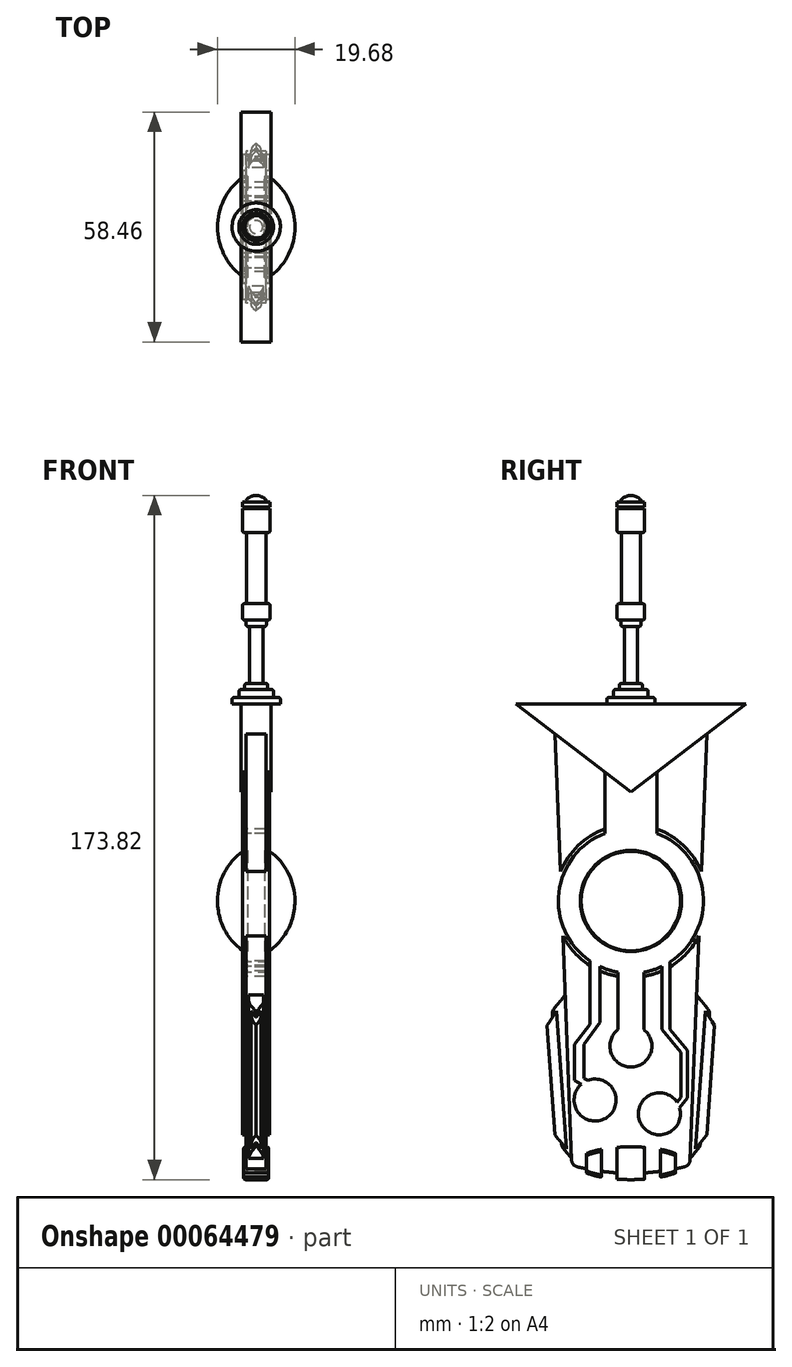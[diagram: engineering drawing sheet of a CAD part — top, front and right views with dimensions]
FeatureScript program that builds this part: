
annotation { "Feature Type Name" : "Feature", "Feature Type Description" : "" }
export const myFeature = defineFeature(function(context is Context, id is Id, definition is map)
    precondition{}
    {
        {
            var Q0;
            Q0=qCreatedBy(makeId("Right.planeOp"),FACE);
            var sketch = newSketch(context, id + "F0", { "sketchPlane" : qUnion([Q0])});
            skLineSegment(sketch, "E0", {"start": v(-29.23, 61.23) * mm, "end": v(0, 61.23) * mm});
            skLineSegment(sketch, "E1", {"start": v(-29.23, 61.23) * mm, "end": v(0, 38.82) * mm});
            skLineSegment(sketch, "E2.MirrorCS", {"start": v(29.23, 61.23) * mm, "end": v(0, 38.82) * mm});
            skLineSegment(sketch, "E3.MirrorCS", {"start": v(29.23, 61.23) * mm, "end": v(0, 61.23) * mm});
            skSolve(sketch);
        }
        {
            var Q0;
            Q0 = qSketchRegion(id + "F0", true);
            var Q1;
            Q1 = qSketchRegion(id + "F13", true);
            extrude(context, id + "F1", {"entities" : qUnion([Q0, Q1]), "endBound" : BoundingType.SYMMETRIC, "depth" : 7.62 * mm});
        }
        {
            var Q0;
            Q0=makeQuery(id+"F1.opExtrude","SWEPT_FACE",FACE,{"disambiguationData":[OSD([sQuery(id+"F0.wireOp",EDGE,"E0"),sQuery(id+"F0.wireOp",EDGE,"E3.MirrorCS")])]});
            var sketch = newSketch(context, id + "F2", { "sketchPlane" : qUnion([Q0])});
            skCircle(sketch, "E4", {"center": v(0, 0) * mm, "radius": 11.71 * mm});
            skSolve(sketch);
        }
        {
            var Q0;
            Q0=qCreatedBy(makeId("Right.planeOp"),FACE);
            var sketch = newSketch(context, id + "F3", { "sketchPlane" : qUnion([Q0])});
            skLineSegment(sketch, "E5", {"start": v(0, -212.2) * mm, "end": v(0, 114.15) * mm});
            skLineSegment(sketch, "E6", {"start": v(-6.14, 61.23) * mm, "end": v(-6.14, 62.83) * mm});
            skLineSegment(sketch, "E7", {"start": v(-6.14, 62.83) * mm, "end": v(-4.4, 62.83) * mm});
            skLineSegment(sketch, "E8", {"start": v(-1.67, 66.45) * mm, "end": v(-1.67, 80.86) * mm});
            skLineSegment(sketch, "E9", {"start": v(-1.67, 80.86) * mm, "end": v(-2.58, 80.86) * mm});
            skLineSegment(sketch, "E10", {"start": v(-2.58, 80.86) * mm, "end": v(-2.58, 82.52) * mm});
            skLineSegment(sketch, "E11", {"start": v(-2.58, 82.52) * mm, "end": v(-3.5, 82.52) * mm});
            skLineSegment(sketch, "E12", {"start": v(-3.5, 82.52) * mm, "end": v(-3.5, 86.7) * mm});
            skLineSegment(sketch, "E13", {"start": v(-3.5, 86.7) * mm, "end": v(-2.45, 86.7) * mm});
            skLineSegment(sketch, "E14", {"start": v(-2.45, 86.7) * mm, "end": v(-2.45, 104.73) * mm});
            skLineSegment(sketch, "E15", {"start": v(-2.45, 104.73) * mm, "end": v(-3.5, 104.73) * mm});
            skLineSegment(sketch, "E16", {"start": v(-3.5, 104.73) * mm, "end": v(-3.5, 110.8) * mm});
            skLineSegment(sketch, "E17", {"start": v(-3.5, 110.8) * mm, "end": v(-2.97, 110.8) * mm});
            skLineSegment(sketch, "E18", {"start": v(-2.97, 110.8) * mm, "end": v(-2.97, 111.21) * mm});
            skLineSegment(sketch, "E19", {"start": v(-2.97, 111.21) * mm, "end": v(-3.5, 111.21) * mm});
            skLineSegment(sketch, "E20", {"start": v(-3.5, 111.21) * mm, "end": v(-3.5, 112.46) * mm});
            skLineSegment(sketch, "E21", {"start": v(-3.5, 112.46) * mm, "end": v(-2.9, 112.46) * mm});
            skArc(sketch, "E22", {"start": v(0, 114.15) * mm, "mid": v(-1.68, 113.7) * mm, "end": v(-2.9, 112.46) * mm});
            skPoint(sketch, "E23.orphan", {"position": v(-3.5, 112.46) * mm});
            skLineSegment(sketch, "E24", {"start": v(-6.14, 61.23) * mm, "end": v(0, 61.23) * mm});
            skLineSegment(sketch, "E25", {"start": v(-2.92, 64.88) * mm, "end": v(-2.92, 66.45) * mm});
            skLineSegment(sketch, "E26", {"start": v(-2.92, 66.45) * mm, "end": v(-1.67, 66.45) * mm});
            skLineSegment(sketch, "E27", {"start": v(-4.4, 62.83) * mm, "end": v(-4.4, 64.88) * mm});
            skLineSegment(sketch, "E28", {"start": v(-4.4, 64.88) * mm, "end": v(-2.92, 64.88) * mm});
            skSolve(sketch);
        }
        {
            var Q0;
            Q0=makeQuery(id+"F3.imprint","IMPRINT",FACE,{"disambiguationData":[TD([[makeQuery(id+"F3.imprint","IMPRINT",EDGE,{"derivedFrom":sQuery(id+"F3.wireOp",EDGE,"E6")}),-1.0]])]});
            var Q1;
            Q1=sQuery(id+"F3.wireOp",EDGE,"E5");
            revolve(context, id + "F4", {"operationType" : NewBodyOperationType.ADD, "entities" : qUnion([Q0]), "axis" : qUnion([Q1]), "revolveType" : RevolveType.FULL});
        }
        {
            var Q0;
            Q0=qCreatedBy(makeId("Right.planeOp"),FACE);
            var sketch = newSketch(context, id + "F5", { "sketchPlane" : qUnion([Q0])});
            skLineSegment(sketch, "E29", {"start": v(-19.3, 53.61) * mm, "end": v(-15, -56.05) * mm});
            skLineSegment(sketch, "E30.MirrorCS", {"start": v(19.3, 53.61) * mm, "end": v(15, -56.05) * mm});
            skLineSegment(sketch, "E31", {"start": v(0, 38.82) * mm, "end": v(-19.3, 53.61) * mm});
            skLineSegment(sketch, "E32", {"start": v(0, 38.82) * mm, "end": v(19.3, 53.61) * mm});
            skArc(sketch, "E33", {"start": v(-15, -56.05) * mm, "mid": v(0, -58.04) * mm, "end": v(15, -56.05) * mm});
            skSolve(sketch);
        }
        {
            var Q0;
            Q0=makeQuery(id+"F5.imprint","IMPRINT",FACE,{"disambiguationData":[TD([[makeQuery(id+"F5.imprint","IMPRINT",EDGE,{"derivedFrom":sQuery(id+"F5.wireOp",EDGE,"E29")}),1.0]])]});
            extrude(context, id + "F6", {"entities" : qUnion([Q0]), "operationType" : NewBodyOperationType.ADD, "endBound" : BoundingType.SYMMETRIC, "depth" : 5.08 * mm});
        }
        {
            var Q0;
            Q0=qCreatedBy(makeId("Right.planeOp"),FACE);
            var sketch = newSketch(context, id + "F7", { "sketchPlane" : qUnion([Q0])});
            skLineSegment(sketch, "E34", {"start": v(-16.7, -12.72) * mm, "end": v(-20.02, -16.87) * mm});
            skLineSegment(sketch, "E35", {"start": v(-20.02, -16.87) * mm, "end": v(-17.57, -51.21) * mm});
            skLineSegment(sketch, "E36", {"start": v(-17.57, -51.21) * mm, "end": v(-15.07, -54.31) * mm});
            skLineSegment(sketch, "E37", {"start": v(-16.7, -12.72) * mm, "end": v(-15.07, -54.31) * mm});
            skLineSegment(sketch, "E38.MirrorCS", {"start": v(16.7, -12.72) * mm, "end": v(20.02, -16.87) * mm});
            skLineSegment(sketch, "E39.MirrorCS", {"start": v(16.7, -12.72) * mm, "end": v(15.07, -54.31) * mm});
            skLineSegment(sketch, "E40.MirrorCS", {"start": v(17.57, -51.21) * mm, "end": v(15.07, -54.31) * mm});
            skLineSegment(sketch, "E41.MirrorCS", {"start": v(20.02, -16.87) * mm, "end": v(17.57, -51.21) * mm});
            skSolve(sketch);
        }
        {
            var Q0;
            Q0 = qSketchRegion(id + "F7", true);
            extrude(context, id + "F8", {"entities" : qUnion([Q0]), "operationType" : NewBodyOperationType.ADD, "endBound" : BoundingType.SYMMETRIC, "depth" : 3.8 * mm});
        }
        {
            var Q0;
            Q0=qCreatedBy(makeId("Right.planeOp"),FACE);
            var sketch = newSketch(context, id + "F9", { "sketchPlane" : qUnion([Q0])});
            skLineSegment(sketch, "E42", {"start": v(-19.9, -18.36) * mm, "end": v(-21.73, -21.25) * mm});
            skLineSegment(sketch, "E43", {"start": v(-19.86, -47.56) * mm, "end": v(-17.64, -50.3) * mm});
            skLineSegment(sketch, "E44", {"start": v(-17.64, -50.3) * mm, "end": v(-19.9, -18.36) * mm});
            skLineSegment(sketch, "E45", {"start": v(-19.86, -47.56) * mm, "end": v(-21.73, -21.25) * mm});
            skLineSegment(sketch, "E46.MirrorCS", {"start": v(19.9, -18.36) * mm, "end": v(21.73, -21.25) * mm});
            skLineSegment(sketch, "E47.MirrorCS", {"start": v(17.64, -50.3) * mm, "end": v(19.9, -18.36) * mm});
            skLineSegment(sketch, "E48.MirrorCS", {"start": v(19.86, -47.56) * mm, "end": v(17.64, -50.3) * mm});
            skLineSegment(sketch, "E49.MirrorCS", {"start": v(19.86, -47.56) * mm, "end": v(21.73, -21.25) * mm});
            skSolve(sketch);
        }
        {
            var Q0;
            Q0=makeQuery(id+"F9.imprint","IMPRINT",FACE,{"disambiguationData":[TD([[makeQuery(id+"F9.imprint","IMPRINT",EDGE,{"derivedFrom":sQuery(id+"F9.wireOp",EDGE,"E42")}),1.0]])]});
            var Q1;
            Q1=makeQuery(id+"F9.imprint","IMPRINT",FACE,{"disambiguationData":[TD([[makeQuery(id+"F9.imprint","IMPRINT",EDGE,{"derivedFrom":sQuery(id+"F9.wireOp",EDGE,"E46.MirrorCS")}),-1.0]])]});
            extrude(context, id + "F10", {"entities" : qUnion([Q0, Q1]), "operationType" : NewBodyOperationType.ADD, "endBound" : BoundingType.SYMMETRIC, "depth" : 2.54 * mm});
        }
        {
            var Q0;
            Q0=qCreatedBy(makeId("Right.planeOp"),FACE);
            var sketch = newSketch(context, id + "F11", { "sketchPlane" : qUnion([Q0])});
            skEllipticalArc(sketch, "E50", {});
            skLineSegment(sketch, "E51", {"start": v(-3.5, -51.45) * mm, "end": v(-3.5, -59.53) * mm});
            skLineSegment(sketch, "E52", {"start": v(0, -51.32) * mm, "end": v(0, -59.66) * mm});
            skLineSegment(sketch, "E53", {"start": v(-7.51, -51.96) * mm, "end": v(-7.51, -59.02) * mm});
            skLineSegment(sketch, "E54", {"start": v(-11.35, -53.04) * mm, "end": v(-11.35, -57.94) * mm});
            skEllipticalArc(sketch, "E55.trimOffspring", {});
            skEllipticalArc(sketch, "E56.trimOffspring", {});
            skEllipticalArc(sketch, "E57.trimOffspring", {});
            skEllipticalArc(sketch, "E58.MirrorCS", {});
            skLineSegment(sketch, "E59.MirrorCS", {"start": v(3.5, -51.45) * mm, "end": v(3.5, -59.53) * mm});
            skEllipticalArc(sketch, "E60.MirrorCS", {});
            skLineSegment(sketch, "E61.MirrorCS", {"start": v(7.51, -51.96) * mm, "end": v(7.51, -59.02) * mm});
            skEllipticalArc(sketch, "E62.MirrorCS", {});
            skLineSegment(sketch, "E63.MirrorCS", {"start": v(11.35, -53.04) * mm, "end": v(11.35, -57.94) * mm});
            skEllipticalArc(sketch, "E64.MirrorCS", {});
            const initialGuessF11  = {"E50": [0, -0.05549049203767605, 1, 0, 0.01403604404596631, 0.004174193487641827, 3.770109793718818, 4.147705169346049], "E55.trimOffspring": [0, -0.05549049203767605, 1, 0, 0.01403604404596631, 0.004174193487641827, 2.135480137833537, 2.5130755134607714], "E56.trimOffspring": [0, -0.05549049203767605, 1, 0, 0.01403604404596631, 0.004174193487641827, 4.460689068859372, 4.71238898038469], "E57.trimOffspring": [0, -0.05549049203767605, 1, 0, 0.01403604404596631, 0.004174193487641827, 1.5707963267948966, 1.8224962383202148], "E58.MirrorCS": [0, -0.05549049203767605, -1, 0, 0.01403604404596631, 0.004174193487641827, 4.460689068859378, 4.71238898038469], "E60.MirrorCS": [0, -0.05549049203767605, -1, 0, 0.01403604404596631, 0.004174193487641827, 1.5707963267948966, 1.822496238320208], "E62.MirrorCS": [0, -0.05549049203767605, -1, 0, 0.01403604404596631, 0.004174193487641827, 3.770109793718824, 4.147705169346056], "E64.MirrorCS": [0, -0.05549049203767605, -1, 0, 0.01403604404596631, 0.004174193487641827, 2.1354801378335297, 2.513075513460759]};
            skSetInitialGuess(sketch, initialGuessF11);
            skSolve(sketch);
        }
        {
            var Q0;
            Q0 = qSketchRegion(id + "F11", true);
            extrude(context, id + "F12", {"entities" : qUnion([Q0]), "operationType" : NewBodyOperationType.ADD, "endBound" : BoundingType.SYMMETRIC, "depth" : 6.35 * mm});
        }
        {
            var Q0;
            Q0=qCreatedBy(makeId("Right.planeOp"),FACE);
            var sketch = newSketch(context, id + "F13", { "sketchPlane" : qUnion([Q0])});
            skCircle(sketch, "E65", {"center": v(0, 11.14) * mm, "radius": 18.41 * mm});
            skLineSegment(sketch, "E66", {"start": v(-6.6, 43.87) * mm, "end": v(-6.6, 28.33) * mm});
            skLineSegment(sketch, "E67.MirrorCS", {"start": v(6.6, 43.87) * mm, "end": v(6.6, 28.33) * mm});
            skLineSegment(sketch, "E68", {"start": v(6.6, 43.87) * mm, "end": v(0, 38.82) * mm});
            skLineSegment(sketch, "E69", {"start": v(0, 38.82) * mm, "end": v(-6.6, 43.87) * mm});
            skSolve(sketch);
        }
        {
            var Q0;
            {var subQ0=sQuery(id+"F5.wireOp",EDGE,"E29");var subQ1=sQuery(id+"F5.wireOp",EDGE,"E33");var subQ2=sQuery(id+"F5.wireOp",EDGE,"E30.MirrorCS");Q0=makeQuery(id+"F19.boolean.opBoolean","SPLIT",FACE,{"disambiguationData":[TD([makeQuery(id+"F6.opExtrude","SWEPT_FACE",FACE,{"disambiguationData":[OSD([subQ1])]})])],"derivedFrom":makeQuery(id+"F6.opExtrude","CAP_FACE",FACE,{"disambiguationData":[OSD([subQ0,subQ2,sQuery(id+"F5.wireOp",EDGE,"E31"),sQuery(id+"F5.wireOp",EDGE,"E32"),subQ1])],"isStart":true})});}
            var sketch = newSketch(context, id + "F14", { "sketchPlane" : qUnion([Q0])});
            skCircle(sketch, "E70", {"center": v(0, 11.14) * mm, "radius": 19.43 * mm});
            skCircle(sketch, "E71", {"center": v(0, 11.14) * mm, "radius": 18.41 * mm});
            skSolve(sketch);
        }
        {
            var Q0;
            Q0 = qSketchRegion(id + "F14", true);
            var Q1;
            {var subQ0=sQuery(id+"F5.wireOp",EDGE,"E29");var subQ1=sQuery(id+"F5.wireOp",EDGE,"E33");var subQ2=sQuery(id+"F5.wireOp",EDGE,"E30.MirrorCS");Q1=makeQuery(id+"F19.boolean.opBoolean","SPLIT",FACE,{"disambiguationData":[TD([makeQuery(id+"F6.opExtrude","SWEPT_FACE",FACE,{"disambiguationData":[OSD([subQ1])]})])],"derivedFrom":makeQuery(id+"F6.opExtrude","CAP_FACE",FACE,{"disambiguationData":[OSD([subQ0,subQ2,sQuery(id+"F5.wireOp",EDGE,"E31"),sQuery(id+"F5.wireOp",EDGE,"E32"),subQ1])],"isStart":false})});}
            extrude(context, id + "F15", {"entities" : qUnion([Q0]), "operationType" : NewBodyOperationType.REMOVE, "endBound" : BoundingType.UP_TO_SURFACE, "oppositeDirection" : true, "endBoundEntityFace" : qUnion([Q1]), "depth" : 25.4 * mm});
        }
        {
            var Q0;
            Q0=qCreatedBy(makeId("Right.planeOp"),FACE);
            var sketch = newSketch(context, id + "F16", { "sketchPlane" : qUnion([Q0])});
            skLineSegment(sketch, "E72", {"start": v(3.3, -6.98) * mm, "end": v(3.3, -21.55) * mm});
            skLineSegment(sketch, "E73.MirrorCS", {"start": v(-3.3, -6.98) * mm, "end": v(-3.3, -21.55) * mm});
            skCircle(sketch, "E74", {"center": v(0, -25.73) * mm, "radius": 5.33 * mm});
            skArc(sketch, "E75", {"start": v(-3.3, -6.98) * mm, "mid": v(0, -7.28) * mm, "end": v(3.3, -6.98) * mm});
            skSolve(sketch);
        }
        {
            var Q0;
            Q0=qCreatedBy(makeId("Right.planeOp"),FACE);
            var sketch = newSketch(context, id + "F17", { "sketchPlane" : qUnion([Q0])});
            skLineSegment(sketch, "E76", {"start": v(-7.83, -5.53) * mm, "end": v(-7.83, -19.77) * mm});
            skLineSegment(sketch, "E77", {"start": v(-7.83, -19.77) * mm, "end": v(-11.97, -25.25) * mm});
            skLineSegment(sketch, "E78", {"start": v(-11.97, -25.25) * mm, "end": v(-11.97, -33.92) * mm});
            skLineSegment(sketch, "E79", {"start": v(-11.97, -33.92) * mm, "end": v(-10.97, -34.46) * mm});
            skLineSegment(sketch, "E80", {"start": v(-12.57, -35.4) * mm, "end": v(-14.32, -34.46) * mm});
            skLineSegment(sketch, "E81", {"start": v(-14.32, -34.46) * mm, "end": v(-14.32, -25.34) * mm});
            skLineSegment(sketch, "E82", {"start": v(-14.32, -25.34) * mm, "end": v(-10.44, -20.2) * mm});
            skLineSegment(sketch, "E83", {"start": v(-10.44, -20.2) * mm, "end": v(-10.44, -4.03) * mm});
            skCircle(sketch, "E84", {"center": v(-9.1, -39.45) * mm, "radius": 5.33 * mm});
            skArc(sketch, "E85", {"start": v(-10.44, -4.03) * mm, "mid": v(-9.17, -4.83) * mm, "end": v(-7.83, -5.53) * mm});
            skSolve(sketch);
        }
        {
            var Q0;
            Q0=qCreatedBy(makeId("Right.planeOp"),FACE);
            var sketch = newSketch(context, id + "F18", { "sketchPlane" : qUnion([Q0])});
            skLineSegment(sketch, "E86", {"start": v(9.94, -4.37) * mm, "end": v(9.94, -21.48) * mm});
            skLineSegment(sketch, "E87", {"start": v(9.94, -21.48) * mm, "end": v(14.37, -26.82) * mm});
            skLineSegment(sketch, "E88", {"start": v(14.37, -26.82) * mm, "end": v(14.37, -38.92) * mm});
            skLineSegment(sketch, "E89", {"start": v(14.37, -38.92) * mm, "end": v(12.38, -41.43) * mm});
            skLineSegment(sketch, "E90", {"start": v(7.83, -5.53) * mm, "end": v(7.83, -21.48) * mm});
            skLineSegment(sketch, "E91", {"start": v(7.83, -21.48) * mm, "end": v(12.72, -27.37) * mm});
            skLineSegment(sketch, "E92", {"start": v(12.72, -27.37) * mm, "end": v(12.72, -38.73) * mm});
            skLineSegment(sketch, "E93", {"start": v(12.72, -38.73) * mm, "end": v(11.7, -40) * mm});
            skCircle(sketch, "E94", {"center": v(7.26, -42.94) * mm, "radius": 5.33 * mm});
            skLineSegment(sketch, "E95", {"start": v(0, -6.18) * mm, "end": v(0, -27.84) * mm, "construction": true});
            skArc(sketch, "E96", {"start": v(7.83, -5.53) * mm, "mid": v(8.9, -4.98) * mm, "end": v(9.94, -4.37) * mm});
            skSolve(sketch);
        }
        {
            var Q0;
            Q0 = qSketchRegion(id + "F18", true);
            var Q1;
            Q1 = qSketchRegion(id + "F17", true);
            var Q2;
            Q2 = qSketchRegion(id + "F16", true);
            var Q3;
            Q3 = qSketchRegion(id + "F13", true);
            extrude(context, id + "F19", {"entities" : qUnion([Q0, Q1, Q2, Q3]), "operationType" : NewBodyOperationType.ADD, "endBound" : BoundingType.SYMMETRIC, "depth" : 6.86 * mm});
        }
        {
            var Q0;
            Q0=makeQuery(id+"F19.boolean.opBoolean","MERGE",FACE,{"derivedFrom":[makeQuery(id+"F19.opExtrude","CAP_FACE",FACE,{"disambiguationData":[OSD([sQuery(id+"F13.wireOp",EDGE,"E65"),sQuery(id+"F13.wireOp",EDGE,"E66"),sQuery(id+"F13.wireOp",EDGE,"E67.MirrorCS"),sQuery(id+"F13.wireOp",EDGE,"E68"),sQuery(id+"F13.wireOp",EDGE,"E69")])],"isStart":false}),makeQuery(id+"F19.opExtrude","CAP_FACE",FACE,{"disambiguationData":[OSD([sQuery(id+"F16.wireOp",EDGE,"E72"),sQuery(id+"F16.wireOp",EDGE,"E73.MirrorCS"),sQuery(id+"F16.wireOp",EDGE,"E74"),sQuery(id+"F16.wireOp",EDGE,"E75")])],"isStart":false}),makeQuery(id+"F19.opExtrude","CAP_FACE",FACE,{"disambiguationData":[OSD([sQuery(id+"F17.wireOp",EDGE,"E76"),sQuery(id+"F17.wireOp",EDGE,"E77"),sQuery(id+"F17.wireOp",EDGE,"E78"),sQuery(id+"F17.wireOp",EDGE,"E79"),sQuery(id+"F17.wireOp",EDGE,"E80"),sQuery(id+"F17.wireOp",EDGE,"E81"),sQuery(id+"F17.wireOp",EDGE,"E82"),sQuery(id+"F17.wireOp",EDGE,"E83"),sQuery(id+"F17.wireOp",EDGE,"E84"),sQuery(id+"F17.wireOp",EDGE,"E85")])],"isStart":false}),makeQuery(id+"F19.opExtrude","CAP_FACE",FACE,{"disambiguationData":[OSD([sQuery(id+"F18.wireOp",EDGE,"E86"),sQuery(id+"F18.wireOp",EDGE,"E87"),sQuery(id+"F18.wireOp",EDGE,"E88"),sQuery(id+"F18.wireOp",EDGE,"E89"),sQuery(id+"F18.wireOp",EDGE,"E90"),sQuery(id+"F18.wireOp",EDGE,"E91"),sQuery(id+"F18.wireOp",EDGE,"E92"),sQuery(id+"F18.wireOp",EDGE,"E93"),sQuery(id+"F18.wireOp",EDGE,"E94"),sQuery(id+"F18.wireOp",EDGE,"E96")])],"isStart":false})]});
            var sketch = newSketch(context, id + "F20", { "sketchPlane" : qUnion([Q0])});
            skCircle(sketch, "E97", {"center": v(0, 11.14) * mm, "radius": 12.64 * mm});
            skSolve(sketch);
        }
        {
            var Q0;
            Q0=qCreatedBy(makeId("Front.planeOp"),FACE);
            var sketch = newSketch(context, id + "F21", { "sketchPlane" : qUnion([Q0])});
            skLineSegment(sketch, "E98", {"start": v(3.43, -1.5) * mm, "end": v(3.43, 11.14) * mm});
            skLineSegment(sketch, "E99", {"start": v(3.43, 11.14) * mm, "end": v(9.84, 11.14) * mm});
            skArc(sketch, "E100", {"start": v(3.43, -1.5) * mm, "mid": v(8.14, 4.05) * mm, "end": v(9.84, 11.14) * mm});
            skSolve(sketch);
        }
        {
            var Q0;
            Q0=makeQuery(id+"F21.imprint","IMPRINT",FACE,{"disambiguationData":[TD([[makeQuery(id+"F21.imprint","IMPRINT",EDGE,{"derivedFrom":sQuery(id+"F21.wireOp",EDGE,"E98")}),-1.0]])]});
            var Q1;
            Q1=sQuery(id+"F21.wireOp",EDGE,"E99");
            revolve(context, id + "F22", {"entities" : qUnion([Q0]), "axis" : qUnion([Q1]), "revolveType" : RevolveType.FULL});
        }
        {
            var Q0;
            Q0=makeQuery(id+"F22.opRevolve","SWEPT_BODY",BODY,{"disambiguationData":[OSD([sQuery(id+"F21.wireOp",EDGE,"E98"),sQuery(id+"F21.wireOp",EDGE,"E99"),sQuery(id+"F21.wireOp",EDGE,"E100")])]});
            var Q1;
            Q1=qCreatedBy(makeId("Right.planeOp"),FACE);
            mirror(context, id + "F23", {"operationType" : NewBodyOperationType.ADD, "entities" : qUnion([Q0]), "mirrorPlane" : qUnion([Q1])});
        }
        {
            var Q0;
            Q0=makeQuery(id+"F19.boolean.opBoolean","MERGE",FACE,{"derivedFrom":[makeQuery(id+"F19.opExtrude","CAP_FACE",FACE,{"disambiguationData":[OSD([sQuery(id+"F13.wireOp",EDGE,"E65"),sQuery(id+"F13.wireOp",EDGE,"E66"),sQuery(id+"F13.wireOp",EDGE,"E67.MirrorCS"),sQuery(id+"F13.wireOp",EDGE,"E68"),sQuery(id+"F13.wireOp",EDGE,"E69")])],"isStart":true}),makeQuery(id+"F19.opExtrude","CAP_FACE",FACE,{"disambiguationData":[OSD([sQuery(id+"F16.wireOp",EDGE,"E72"),sQuery(id+"F16.wireOp",EDGE,"E73.MirrorCS"),sQuery(id+"F16.wireOp",EDGE,"E74"),sQuery(id+"F16.wireOp",EDGE,"E75")])],"isStart":true}),makeQuery(id+"F19.opExtrude","CAP_FACE",FACE,{"disambiguationData":[OSD([sQuery(id+"F17.wireOp",EDGE,"E76"),sQuery(id+"F17.wireOp",EDGE,"E77"),sQuery(id+"F17.wireOp",EDGE,"E78"),sQuery(id+"F17.wireOp",EDGE,"E79"),sQuery(id+"F17.wireOp",EDGE,"E80"),sQuery(id+"F17.wireOp",EDGE,"E81"),sQuery(id+"F17.wireOp",EDGE,"E82"),sQuery(id+"F17.wireOp",EDGE,"E83"),sQuery(id+"F17.wireOp",EDGE,"E84"),sQuery(id+"F17.wireOp",EDGE,"E85")])],"isStart":true}),makeQuery(id+"F19.opExtrude","CAP_FACE",FACE,{"disambiguationData":[OSD([sQuery(id+"F18.wireOp",EDGE,"E86"),sQuery(id+"F18.wireOp",EDGE,"E87"),sQuery(id+"F18.wireOp",EDGE,"E88"),sQuery(id+"F18.wireOp",EDGE,"E89"),sQuery(id+"F18.wireOp",EDGE,"E90"),sQuery(id+"F18.wireOp",EDGE,"E91"),sQuery(id+"F18.wireOp",EDGE,"E92"),sQuery(id+"F18.wireOp",EDGE,"E93"),sQuery(id+"F18.wireOp",EDGE,"E94"),sQuery(id+"F18.wireOp",EDGE,"E96")])],"isStart":true})]});
            var sketch = newSketch(context, id + "F24", { "sketchPlane" : qUnion([Q0])});
            skCircle(sketch, "E101", {"center": v(0, 11.14) * mm, "radius": 12.87 * mm});
            skCircle(sketch, "E102.0", {"center": v(0, 11.14) * mm, "radius": 12.64 * mm});
            skSolve(sketch);
        }
        {
            var Q0;
            Q0 = qSketchRegion(id + "F24", true);
            extrude(context, id + "F25", {"entities" : qUnion([Q0]), "oppositeDirection" : true, "depth" : 1.27 * mm});
        }
        {
            var Q0;
            Q0=makeQuery(id+"F25.opExtrude","SWEPT_BODY",BODY,{"disambiguationData":[OSD([sQuery(id+"F24.wireOp",EDGE,"E101"),sQuery(id+"F24.wireOp",EDGE,"E102.0")])]});
            var Q1;
            Q1=qCreatedBy(makeId("Right.planeOp"),FACE);
            mirror(context, id + "F26", {"operationType" : NewBodyOperationType.REMOVE, "entities" : qUnion([Q0]), "mirrorPlane" : qUnion([Q1])});
        }
        {
            var Q0;
            Q0=makeQuery(id+"F25.opExtrude","SWEPT_BODY",BODY,{"disambiguationData":[OSD([sQuery(id+"F24.wireOp",EDGE,"E101"),sQuery(id+"F24.wireOp",EDGE,"E102.0")])]});
            var Q1;
            Q1=makeQuery(id+"F1.opExtrude","SWEPT_BODY",BODY,{"disambiguationData":[OSD([sQuery(id+"F0.wireOp",EDGE,"E0"),sQuery(id+"F0.wireOp",EDGE,"E2.MirrorCS"),sQuery(id+"F0.wireOp",EDGE,"E1"),sQuery(id+"F0.wireOp",EDGE,"E3.MirrorCS")])]});
            booleanBodies(context, id + "F27", {"operationType" : BooleanOperationType.SUBTRACTION, "tools" : qUnion([Q0]), "targets" : qUnion([Q1])});
        }
        {
            var Q0;
            Q0=makeQuery(id+"F12.opExtrude","CAP_EDGE",EDGE,{"disambiguationData":[OSD([sQuery(id+"F11.wireOp",EDGE,"E56.trimOffspring"),sQuery(id+"F11.wireOp",EDGE,"E60.MirrorCS")])],"isStart":false});
            var Q1;
            Q1=makeQuery(id+"F12.opExtrude","CAP_EDGE",EDGE,{"disambiguationData":[OSD([sQuery(id+"F11.wireOp",EDGE,"E64.MirrorCS")])],"isStart":false});
            var Q2;
            Q2=makeQuery(id+"F12.opExtrude","CAP_EDGE",EDGE,{"disambiguationData":[OSD([sQuery(id+"F11.wireOp",EDGE,"E50")])],"isStart":false});
            var Q3;
            Q3=makeQuery(id+"F12.opExtrude","CAP_EDGE",EDGE,{"disambiguationData":[OSD([sQuery(id+"F11.wireOp",EDGE,"E64.MirrorCS")])],"isStart":true});
            var Q4;
            Q4=makeQuery(id+"F12.opExtrude","CAP_EDGE",EDGE,{"disambiguationData":[OSD([sQuery(id+"F11.wireOp",EDGE,"E56.trimOffspring"),sQuery(id+"F11.wireOp",EDGE,"E60.MirrorCS")])],"isStart":true});
            var Q5;
            Q5=makeQuery(id+"F12.opExtrude","CAP_EDGE",EDGE,{"disambiguationData":[OSD([sQuery(id+"F11.wireOp",EDGE,"E50")])],"isStart":true});
            var Q6;
            Q6=makeQuery(id+"F12.opExtrude","CAP_EDGE",EDGE,{"disambiguationData":[OSD([sQuery(id+"F11.wireOp",EDGE,"E55.trimOffspring")])],"isStart":false});
            var Q7;
            Q7=makeQuery(id+"F12.opExtrude","CAP_EDGE",EDGE,{"disambiguationData":[OSD([sQuery(id+"F11.wireOp",EDGE,"E57.trimOffspring"),sQuery(id+"F11.wireOp",EDGE,"E58.MirrorCS")])],"isStart":false});
            var Q8;
            Q8=makeQuery(id+"F12.opExtrude","CAP_EDGE",EDGE,{"disambiguationData":[OSD([sQuery(id+"F11.wireOp",EDGE,"E62.MirrorCS")])],"isStart":false});
            var Q9;
            Q9=makeQuery(id+"F12.opExtrude","CAP_EDGE",EDGE,{"disambiguationData":[OSD([sQuery(id+"F11.wireOp",EDGE,"E55.trimOffspring")])],"isStart":true});
            var Q10;
            Q10=makeQuery(id+"F12.opExtrude","CAP_EDGE",EDGE,{"disambiguationData":[OSD([sQuery(id+"F11.wireOp",EDGE,"E57.trimOffspring"),sQuery(id+"F11.wireOp",EDGE,"E58.MirrorCS")])],"isStart":true});
            var Q11;
            Q11=makeQuery(id+"F12.opExtrude","CAP_EDGE",EDGE,{"disambiguationData":[OSD([sQuery(id+"F11.wireOp",EDGE,"E62.MirrorCS")])],"isStart":true});
            fillet(context, id + "F28", {"entities" : qUnion([Q0, Q1, Q2, Q3, Q4, Q5, Q6, Q7, Q8, Q9, Q10, Q11]), "radius" : 0.5 * mm, "tangentPropagation" : true, "allowEdgeOverflow" : false});
        }
        {
            var Q0;
            Q0=makeQuery(id+"F10.opExtrude","CAP_EDGE",EDGE,{"disambiguationData":[OSD([sQuery(id+"F9.wireOp",EDGE,"E45")])],"isStart":true});
            var Q1;
            Q1=makeQuery(id+"F10.opExtrude","CAP_EDGE",EDGE,{"disambiguationData":[OSD([sQuery(id+"F9.wireOp",EDGE,"E45")])],"isStart":false});
            var Q2;
            Q2=makeQuery(id+"F10.opExtrude","CAP_EDGE",EDGE,{"disambiguationData":[OSD([sQuery(id+"F9.wireOp",EDGE,"E49.MirrorCS")])],"isStart":true});
            var Q3;
            Q3=makeQuery(id+"F10.opExtrude","CAP_EDGE",EDGE,{"disambiguationData":[OSD([sQuery(id+"F9.wireOp",EDGE,"E49.MirrorCS")])],"isStart":false});
            var Q4;
            Q4=makeQuery(id+"F8.opExtrude","CAP_EDGE",EDGE,{"disambiguationData":[OSD([sQuery(id+"F7.wireOp",EDGE,"E35")])],"isStart":false});
            var Q5;
            Q5=makeQuery(id+"F8.opExtrude","CAP_EDGE",EDGE,{"disambiguationData":[OSD([sQuery(id+"F7.wireOp",EDGE,"E35")])],"isStart":true});
            var Q6;
            Q6=makeQuery(id+"F8.opExtrude","CAP_EDGE",EDGE,{"disambiguationData":[OSD([sQuery(id+"F7.wireOp",EDGE,"E41.MirrorCS")])],"isStart":true});
            var Q7;
            Q7=makeQuery(id+"F8.opExtrude","CAP_EDGE",EDGE,{"disambiguationData":[OSD([sQuery(id+"F7.wireOp",EDGE,"E41.MirrorCS")])],"isStart":false});
            chamfer(context, id + "F29", {"entities" : qUnion([Q0, Q1, Q2, Q3, Q4, Q5, Q6, Q7]), "chamferType" : ChamferType.OFFSET_ANGLE, "width" : 1.78 * mm, "oppositeDirection" : true, "angle" : 45 * degree, "tangentPropagation" : true});
        }
        {
            var Q0;
            Q0=makeQuery(id+"F4.opRevolve","SWEPT_FACE",FACE,{"disambiguationData":[OSD([sQuery(id+"F3.wireOp",EDGE,"E27")])]});
            var Q1;
            Q1=makeQuery(id+"F4.opRevolve","SWEPT_EDGE",EDGE,{"disambiguationData":[OSD([sQuery(id+"F3.wireOp",EDGE,"E6"),sQuery(id+"F3.wireOp",EDGE,"E7")])]});
            var Q2;
            Q2=makeQuery(id+"F4.opRevolve","SWEPT_EDGE",EDGE,{"disambiguationData":[OSD([sQuery(id+"F3.wireOp",EDGE,"E25"),sQuery(id+"F3.wireOp",EDGE,"E26")])]});
            var Q3;
            Q3=makeQuery(id+"F4.opRevolve","SWEPT_EDGE",EDGE,{"disambiguationData":[OSD([sQuery(id+"F3.wireOp",EDGE,"E12"),sQuery(id+"F3.wireOp",EDGE,"E13")])]});
            var Q4;
            Q4=makeQuery(id+"F4.opRevolve","SWEPT_EDGE",EDGE,{"disambiguationData":[OSD([sQuery(id+"F3.wireOp",EDGE,"E11"),sQuery(id+"F3.wireOp",EDGE,"E12")])]});
            var Q5;
            Q5=makeQuery(id+"F4.opRevolve","SWEPT_EDGE",EDGE,{"disambiguationData":[OSD([sQuery(id+"F3.wireOp",EDGE,"E15"),sQuery(id+"F3.wireOp",EDGE,"E16")])]});
            var Q6;
            Q6=makeQuery(id+"F4.opRevolve","SWEPT_EDGE",EDGE,{"disambiguationData":[OSD([sQuery(id+"F3.wireOp",EDGE,"E9"),sQuery(id+"F3.wireOp",EDGE,"E10")])]});
            fillet(context, id + "F30", {"entities" : qUnion([Q0, Q1, Q2, Q3, Q4, Q5, Q6]), "radius" : 0.5 * mm, "tangentPropagation" : true, "allowEdgeOverflow" : false});
        }
        {
            var Q0;
            Q0=makeQuery(id+"F6.opExtrude","SWEPT_EDGE",EDGE,{"disambiguationData":[OSD([sQuery(id+"F5.wireOp",EDGE,"E29"),sQuery(id+"F5.wireOp",EDGE,"E33")])]});
            var Q1;
            Q1=makeQuery(id+"F6.opExtrude","SWEPT_EDGE",EDGE,{"disambiguationData":[OSD([sQuery(id+"F5.wireOp",EDGE,"E30.MirrorCS"),sQuery(id+"F5.wireOp",EDGE,"E33")])]});
            var Q2;
            Q2=makeQuery(id+"F8.opExtrude","SWEPT_EDGE",EDGE,{"disambiguationData":[OSD([sQuery(id+"F7.wireOp",EDGE,"E40.MirrorCS"),sQuery(id+"F7.wireOp",EDGE,"E41.MirrorCS")])]});
            var Q3;
            Q3=makeQuery(id+"F8.opExtrude","SWEPT_EDGE",EDGE,{"disambiguationData":[OSD([sQuery(id+"F7.wireOp",EDGE,"E34"),sQuery(id+"F7.wireOp",EDGE,"E35")])]});
            var Q4;
            Q4=makeQuery(id+"F8.opExtrude","SWEPT_EDGE",EDGE,{"disambiguationData":[OSD([sQuery(id+"F7.wireOp",EDGE,"E38.MirrorCS"),sQuery(id+"F7.wireOp",EDGE,"E41.MirrorCS")])]});
            var Q5;
            Q5=makeQuery(id+"F8.opExtrude","SWEPT_EDGE",EDGE,{"disambiguationData":[OSD([sQuery(id+"F7.wireOp",EDGE,"E35"),sQuery(id+"F7.wireOp",EDGE,"E36")])]});
            var Q6;
            {var subQ0=sQuery(id+"F7.wireOp",EDGE,"E35");Q6=makeQuery(id+"F29.opChamfer","BLEND_EDGE",EDGE,{"blendedFrom":[makeQuery(id+"F8.opExtrude","CAP_EDGE",EDGE,{"disambiguationData":[OSD([subQ0])],"isStart":true}),makeQuery(id+"F8.opExtrude","CAP_FACE",FACE,{"disambiguationData":[OSD([sQuery(id+"F7.wireOp",EDGE,"E34"),subQ0,sQuery(id+"F7.wireOp",EDGE,"E36"),sQuery(id+"F7.wireOp",EDGE,"E37")])],"isStart":true})],"blendedInto":[makeQuery(id+"F8.opExtrude","CAP_FACE",FACE,{"disambiguationData":[OSD([sQuery(id+"F7.wireOp",EDGE,"E34"),subQ0,sQuery(id+"F7.wireOp",EDGE,"E36"),sQuery(id+"F7.wireOp",EDGE,"E37")])],"isStart":true})]});}
            var Q7;
            {var subQ0=sQuery(id+"F9.wireOp",EDGE,"E45");Q7=makeQuery(id+"F29.opChamfer","BLEND_EDGE",EDGE,{"blendedFrom":[makeQuery(id+"F10.opExtrude","CAP_EDGE",EDGE,{"disambiguationData":[OSD([subQ0])],"isStart":true}),makeQuery(id+"F10.opExtrude","CAP_FACE",FACE,{"disambiguationData":[OSD([sQuery(id+"F9.wireOp",EDGE,"E42"),sQuery(id+"F9.wireOp",EDGE,"E43"),sQuery(id+"F9.wireOp",EDGE,"E44"),subQ0])],"isStart":true})],"blendedInto":[makeQuery(id+"F10.opExtrude","CAP_FACE",FACE,{"disambiguationData":[OSD([sQuery(id+"F9.wireOp",EDGE,"E42"),sQuery(id+"F9.wireOp",EDGE,"E43"),sQuery(id+"F9.wireOp",EDGE,"E44"),subQ0])],"isStart":true})]});}
            var Q8;
            {var subQ0=sQuery(id+"F9.wireOp",EDGE,"E45");Q8=makeQuery(id+"F29.opChamfer","BLEND_EDGE",EDGE,{"blendedFrom":[makeQuery(id+"F10.opExtrude","CAP_EDGE",EDGE,{"disambiguationData":[OSD([subQ0])],"isStart":false}),makeQuery(id+"F10.opExtrude","CAP_FACE",FACE,{"disambiguationData":[OSD([sQuery(id+"F9.wireOp",EDGE,"E42"),sQuery(id+"F9.wireOp",EDGE,"E43"),sQuery(id+"F9.wireOp",EDGE,"E44"),subQ0])],"isStart":false})],"blendedInto":[makeQuery(id+"F10.opExtrude","CAP_FACE",FACE,{"disambiguationData":[OSD([sQuery(id+"F9.wireOp",EDGE,"E42"),sQuery(id+"F9.wireOp",EDGE,"E43"),sQuery(id+"F9.wireOp",EDGE,"E44"),subQ0])],"isStart":false})]});}
            var Q9;
            {var subQ0=sQuery(id+"F7.wireOp",EDGE,"E35");Q9=makeQuery(id+"F29.opChamfer","BLEND_EDGE",EDGE,{"blendedFrom":[makeQuery(id+"F8.opExtrude","CAP_EDGE",EDGE,{"disambiguationData":[OSD([subQ0])],"isStart":false}),makeQuery(id+"F8.opExtrude","CAP_FACE",FACE,{"disambiguationData":[OSD([sQuery(id+"F7.wireOp",EDGE,"E34"),subQ0,sQuery(id+"F7.wireOp",EDGE,"E36"),sQuery(id+"F7.wireOp",EDGE,"E37")])],"isStart":false})],"blendedInto":[makeQuery(id+"F8.opExtrude","CAP_FACE",FACE,{"disambiguationData":[OSD([sQuery(id+"F7.wireOp",EDGE,"E34"),subQ0,sQuery(id+"F7.wireOp",EDGE,"E36"),sQuery(id+"F7.wireOp",EDGE,"E37")])],"isStart":false})]});}
            var Q10;
            {var subQ0=sQuery(id+"F7.wireOp",EDGE,"E41.MirrorCS");Q10=makeQuery(id+"F29.opChamfer","BLEND_EDGE",EDGE,{"blendedFrom":[makeQuery(id+"F8.opExtrude","CAP_EDGE",EDGE,{"disambiguationData":[OSD([subQ0])],"isStart":true}),makeQuery(id+"F8.opExtrude","CAP_FACE",FACE,{"disambiguationData":[OSD([sQuery(id+"F7.wireOp",EDGE,"E38.MirrorCS"),sQuery(id+"F7.wireOp",EDGE,"E39.MirrorCS"),sQuery(id+"F7.wireOp",EDGE,"E40.MirrorCS"),subQ0])],"isStart":true})],"blendedInto":[makeQuery(id+"F8.opExtrude","CAP_FACE",FACE,{"disambiguationData":[OSD([sQuery(id+"F7.wireOp",EDGE,"E38.MirrorCS"),sQuery(id+"F7.wireOp",EDGE,"E39.MirrorCS"),sQuery(id+"F7.wireOp",EDGE,"E40.MirrorCS"),subQ0])],"isStart":true})]});}
            var Q11;
            {var subQ0=sQuery(id+"F9.wireOp",EDGE,"E49.MirrorCS");Q11=makeQuery(id+"F29.opChamfer","BLEND_EDGE",EDGE,{"blendedFrom":[makeQuery(id+"F10.opExtrude","CAP_EDGE",EDGE,{"disambiguationData":[OSD([subQ0])],"isStart":true}),makeQuery(id+"F10.opExtrude","CAP_FACE",FACE,{"disambiguationData":[OSD([sQuery(id+"F9.wireOp",EDGE,"E46.MirrorCS"),sQuery(id+"F9.wireOp",EDGE,"E47.MirrorCS"),sQuery(id+"F9.wireOp",EDGE,"E48.MirrorCS"),subQ0])],"isStart":true})],"blendedInto":[makeQuery(id+"F10.opExtrude","CAP_FACE",FACE,{"disambiguationData":[OSD([sQuery(id+"F9.wireOp",EDGE,"E46.MirrorCS"),sQuery(id+"F9.wireOp",EDGE,"E47.MirrorCS"),sQuery(id+"F9.wireOp",EDGE,"E48.MirrorCS"),subQ0])],"isStart":true})]});}
            var Q12;
            {var subQ0=sQuery(id+"F9.wireOp",EDGE,"E49.MirrorCS");Q12=makeQuery(id+"F29.opChamfer","BLEND_EDGE",EDGE,{"blendedFrom":[makeQuery(id+"F10.opExtrude","CAP_EDGE",EDGE,{"disambiguationData":[OSD([subQ0])],"isStart":false}),makeQuery(id+"F10.opExtrude","CAP_FACE",FACE,{"disambiguationData":[OSD([sQuery(id+"F9.wireOp",EDGE,"E46.MirrorCS"),sQuery(id+"F9.wireOp",EDGE,"E47.MirrorCS"),sQuery(id+"F9.wireOp",EDGE,"E48.MirrorCS"),subQ0])],"isStart":false})],"blendedInto":[makeQuery(id+"F10.opExtrude","CAP_FACE",FACE,{"disambiguationData":[OSD([sQuery(id+"F9.wireOp",EDGE,"E46.MirrorCS"),sQuery(id+"F9.wireOp",EDGE,"E47.MirrorCS"),sQuery(id+"F9.wireOp",EDGE,"E48.MirrorCS"),subQ0])],"isStart":false})]});}
            var Q13;
            {var subQ0=sQuery(id+"F7.wireOp",EDGE,"E41.MirrorCS");Q13=makeQuery(id+"F29.opChamfer","BLEND_EDGE",EDGE,{"blendedFrom":[makeQuery(id+"F8.opExtrude","CAP_EDGE",EDGE,{"disambiguationData":[OSD([subQ0])],"isStart":false}),makeQuery(id+"F8.opExtrude","CAP_FACE",FACE,{"disambiguationData":[OSD([sQuery(id+"F7.wireOp",EDGE,"E38.MirrorCS"),sQuery(id+"F7.wireOp",EDGE,"E39.MirrorCS"),sQuery(id+"F7.wireOp",EDGE,"E40.MirrorCS"),subQ0])],"isStart":false})],"blendedInto":[makeQuery(id+"F8.opExtrude","CAP_FACE",FACE,{"disambiguationData":[OSD([sQuery(id+"F7.wireOp",EDGE,"E38.MirrorCS"),sQuery(id+"F7.wireOp",EDGE,"E39.MirrorCS"),sQuery(id+"F7.wireOp",EDGE,"E40.MirrorCS"),subQ0])],"isStart":false})]});}
            fillet(context, id + "F31", {"entities" : qUnion([Q0, Q1, Q2, Q3, Q4, Q5, Q6, Q7, Q8, Q9, Q10, Q11, Q12, Q13]), "radius" : 1.78 * mm, "tangentPropagation" : true, "allowEdgeOverflow" : false});
        }
    });
